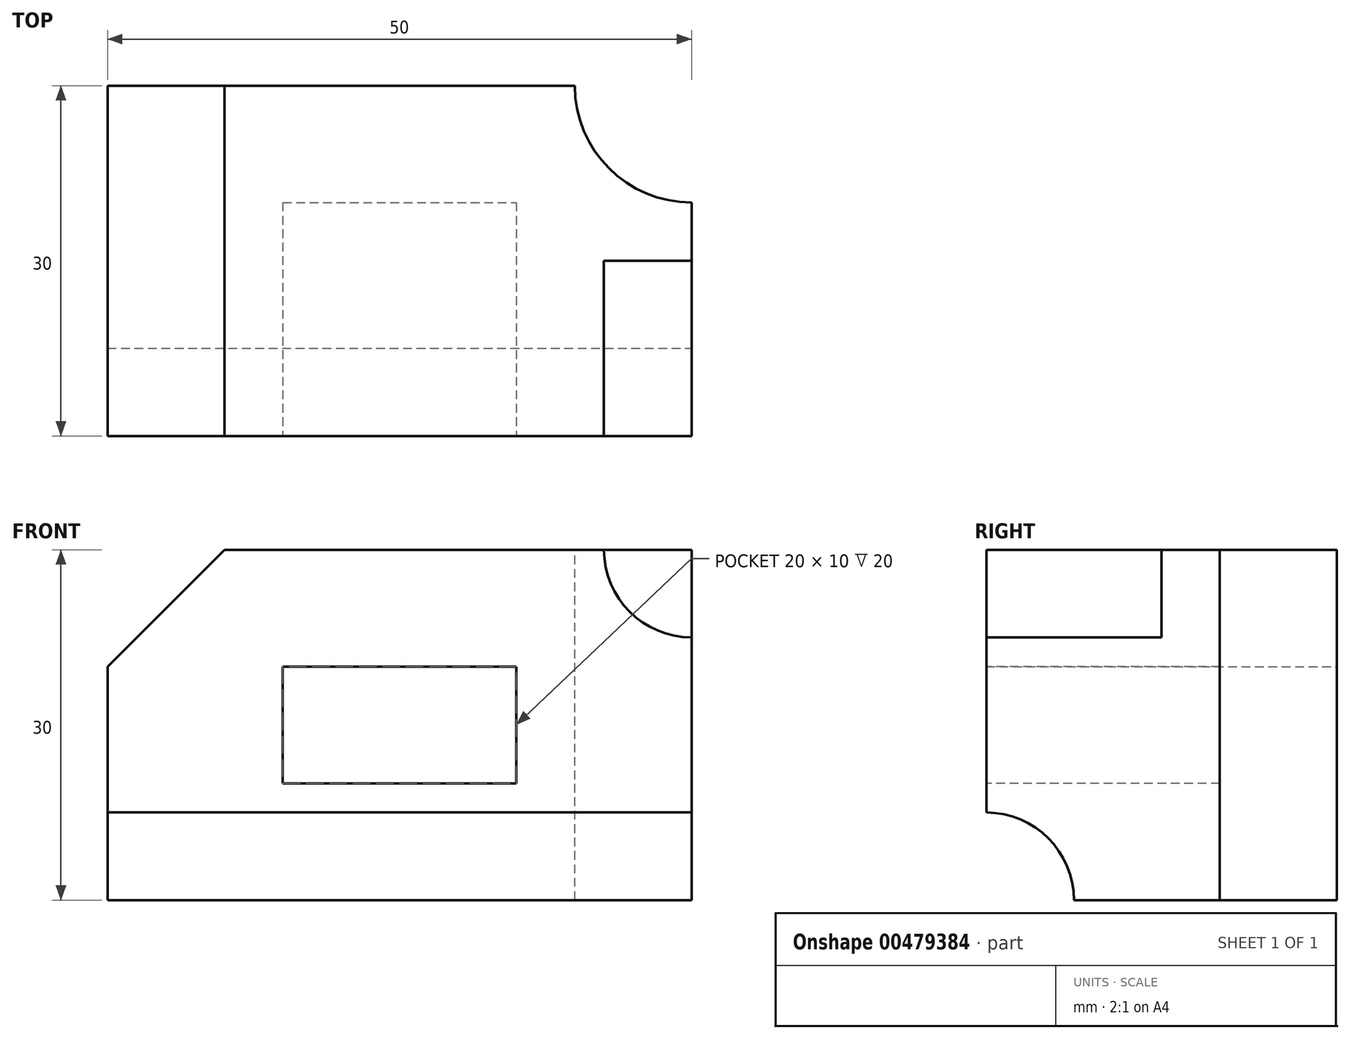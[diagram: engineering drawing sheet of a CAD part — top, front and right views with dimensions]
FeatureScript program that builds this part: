
annotation { "Feature Type Name" : "Feature", "Feature Type Description" : "" }
export const myFeature = defineFeature(function(context is Context, id is Id, definition is map)
    precondition{}
    {
        {
            var Q0;
            Q0=qCreatedBy(makeId("Top.planeOp"),FACE);
            var sketch = newSketch(context, id + "F0", { "sketchPlane" : qUnion([Q0])});
            skLineSegment(sketch, "E0.bottom", {"start": v(0, 0) * mm, "end": v(50, 0) * mm});
            skLineSegment(sketch, "E0.top", {"start": v(0, 30) * mm, "end": v(50, 30) * mm});
            skLineSegment(sketch, "E0.left", {"start": v(0, 0) * mm, "end": v(0, 30) * mm});
            skLineSegment(sketch, "E0.right", {"start": v(50, 0) * mm, "end": v(50, 30) * mm});
            skSolve(sketch);
        }
        {
            var Q0;
            Q0 = qSketchRegion(id + "F0", true);
            extrude(context, id + "F1", {"entities" : qUnion([Q0]), "depth" : 30 * mm});
        }
        {
            var Q0;
            Q0=makeQuery(id+"F1.opExtrude","CAP_EDGE",EDGE,{"disambiguationData":[OSD([sQuery(id+"F0.wireOp",EDGE,"E0.left")])],"isStart":false});
            chamfer(context, id + "F2", {"entities" : qUnion([Q0]), "width" : 10 * mm, "tangentPropagation" : true});
        }
        {
            var Q0;
            Q0=makeQuery(id+"F1.opExtrude","CAP_FACE",FACE,{"disambiguationData":[OSD([sQuery(id+"F0.wireOp",EDGE,"E0.bottom"),sQuery(id+"F0.wireOp",EDGE,"E0.top"),sQuery(id+"F0.wireOp",EDGE,"E0.left"),sQuery(id+"F0.wireOp",EDGE,"E0.right")])],"isStart":false});
            var sketch = newSketch(context, id + "F3", { "sketchPlane" : qUnion([Q0])});
            skCircle(sketch, "E1", {"center": v(50, 30) * mm, "radius": 10 * mm});
            skSolve(sketch);
        }
        {
            var Q0;
            Q0 = qSketchRegion(id + "F3", true);
            extrude(context, id + "F4", {"entities" : qUnion([Q0]), "operationType" : NewBodyOperationType.REMOVE, "endBound" : BoundingType.THROUGH_ALL, "oppositeDirection" : true, "depth" : 25 * mm});
        }
        {
            var Q0;
            Q0=makeQuery(id+"F1.opExtrude","SWEPT_FACE",FACE,{"disambiguationData":[OSD([sQuery(id+"F0.wireOp",EDGE,"E0.right")])]});
            var sketch = newSketch(context, id + "F5", { "sketchPlane" : qUnion([Q0])});
            skCircle(sketch, "E2", {"center": v(0, 0) * mm, "radius": 7.5 * mm});
            skSolve(sketch);
        }
        {
            var Q0;
            Q0 = qSketchRegion(id + "F5", true);
            extrude(context, id + "F6", {"entities" : qUnion([Q0]), "operationType" : NewBodyOperationType.REMOVE, "endBound" : BoundingType.THROUGH_ALL, "oppositeDirection" : true, "depth" : 25 * mm});
        }
        {
            var Q0;
            Q0=makeQuery(id+"F1.opExtrude","SWEPT_FACE",FACE,{"disambiguationData":[OSD([sQuery(id+"F0.wireOp",EDGE,"E0.bottom")])]});
            var sketch = newSketch(context, id + "F7", { "sketchPlane" : qUnion([Q0])});
            skLineSegment(sketch, "E3.bottom", {"start": v(15, 20) * mm, "end": v(35, 20) * mm});
            skLineSegment(sketch, "E3.top", {"start": v(15, 10) * mm, "end": v(35, 10) * mm});
            skLineSegment(sketch, "E3.left", {"start": v(15, 20) * mm, "end": v(15, 10) * mm});
            skLineSegment(sketch, "E3.right", {"start": v(35, 20) * mm, "end": v(35, 10) * mm});
            skSolve(sketch);
        }
        {
            var Q0;
            Q0 = qSketchRegion(id + "F7", true);
            extrude(context, id + "F8", {"entities" : qUnion([Q0]), "operationType" : NewBodyOperationType.REMOVE, "oppositeDirection" : true, "depth" : 20 * mm});
        }
        {
            var Q0;
            Q0=makeQuery(id+"F1.opExtrude","SWEPT_FACE",FACE,{"disambiguationData":[OSD([sQuery(id+"F0.wireOp",EDGE,"E0.bottom")])]});
            var sketch = newSketch(context, id + "F9", { "sketchPlane" : qUnion([Q0])});
            skCircle(sketch, "E4", {"center": v(50, 30) * mm, "radius": 7.5 * mm});
            skSolve(sketch);
        }
        {
            var Q0;
            Q0 = qSketchRegion(id + "F9", true);
            extrude(context, id + "F10", {"entities" : qUnion([Q0]), "operationType" : NewBodyOperationType.REMOVE, "oppositeDirection" : true, "depth" : 15 * mm});
        }
    });
